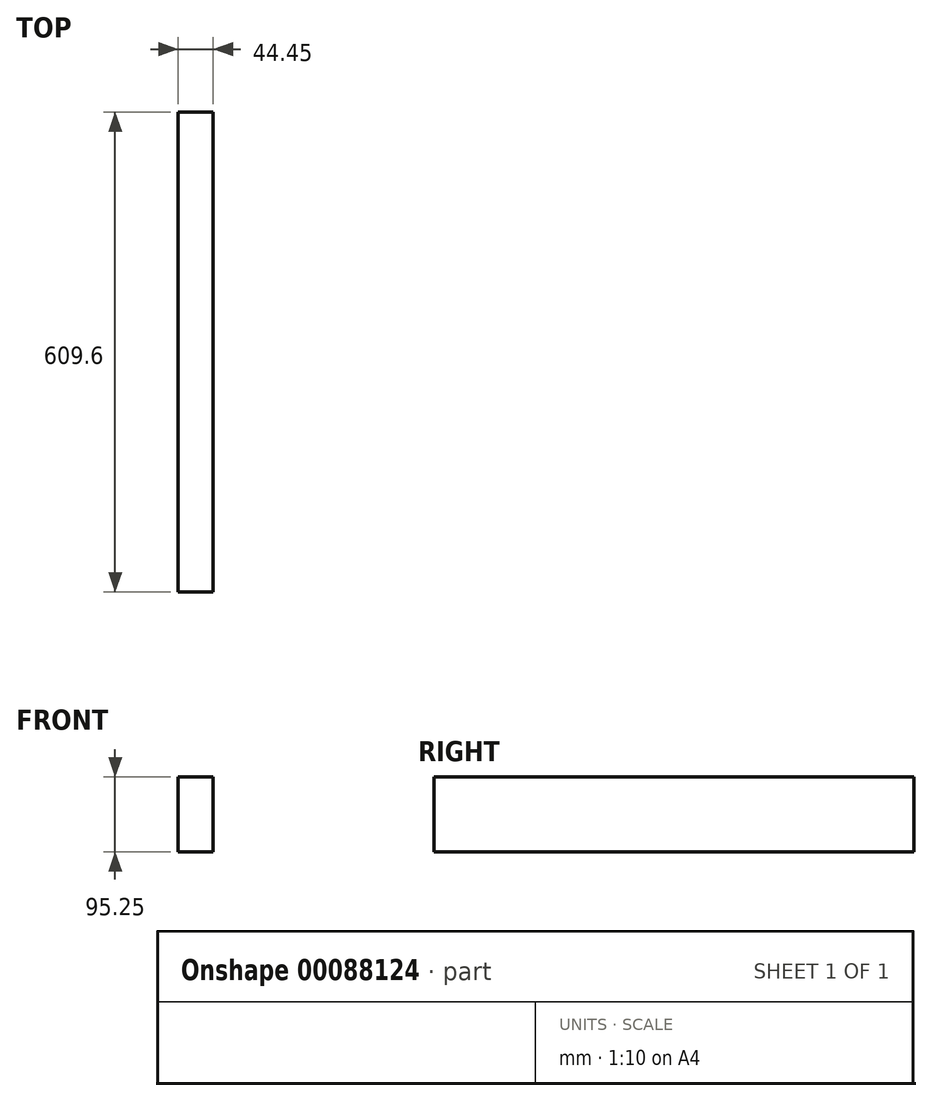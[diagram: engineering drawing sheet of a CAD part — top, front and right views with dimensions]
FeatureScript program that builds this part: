
annotation { "Feature Type Name" : "Feature", "Feature Type Description" : "" }
export const myFeature = defineFeature(function(context is Context, id is Id, definition is map)
    precondition{}
    {
        {
            var Q0;
            Q0=qCreatedBy(makeId("Front.planeOp"),FACE);
            var sketch = newSketch(context, id + "F0", { "sketchPlane" : qUnion([Q0])});
            skLineSegment(sketch, "E0.bottom", {"start": v(0, 0) * mm, "end": v(44.45, 0) * mm});
            skLineSegment(sketch, "E0.top", {"start": v(0, 95.25) * mm, "end": v(44.45, 95.25) * mm});
            skLineSegment(sketch, "E0.left", {"start": v(0, 0) * mm, "end": v(0, 95.25) * mm});
            skLineSegment(sketch, "E0.right", {"start": v(44.45, 0) * mm, "end": v(44.45, 95.25) * mm});
            skSolve(sketch);
        }
        {
            var Q0;
            Q0=makeQuery(id+"F0.imprint","IMPRINT",FACE,{"disambiguationData":[TD([[makeQuery(id+"F0.imprint","IMPRINT",EDGE,{"derivedFrom":sQuery(id+"F0.wireOp",EDGE,"E0.bottom")}),1.0]])]});
            extrude(context, id + "F1", {"entities" : qUnion([Q0]), "depth" : 609.6 * mm});
        }
    });
